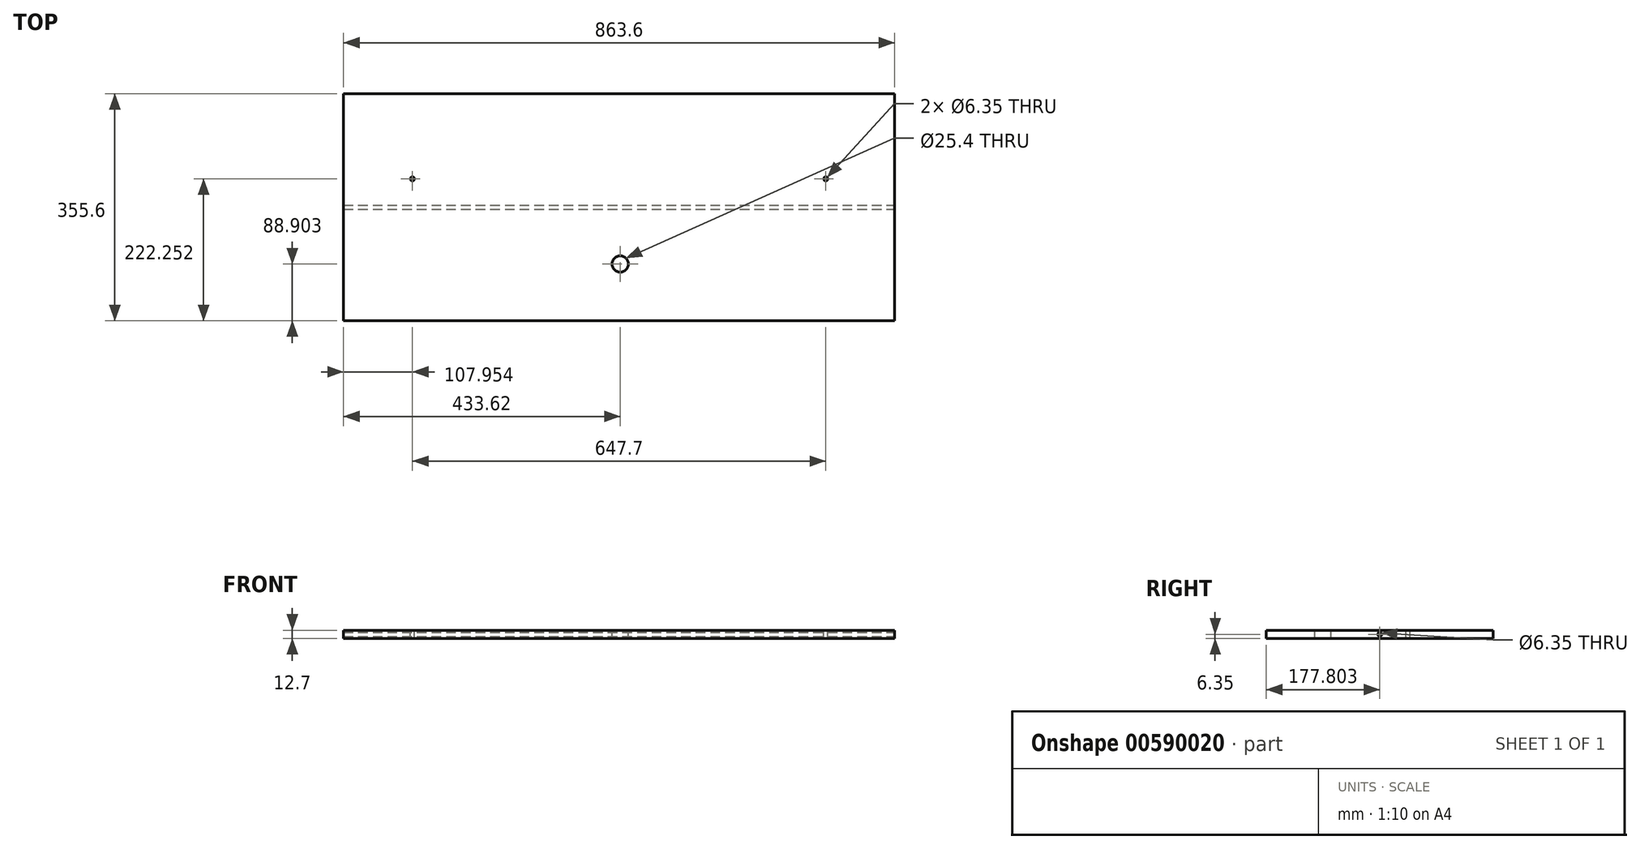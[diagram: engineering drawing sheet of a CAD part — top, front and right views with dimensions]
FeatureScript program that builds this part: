
annotation { "Feature Type Name" : "Feature", "Feature Type Description" : "" }
export const myFeature = defineFeature(function(context is Context, id is Id, definition is map)
    precondition{}
    {
        {
            var Q0;
            Q0=qCreatedBy(makeId("Top.planeOp"),FACE);
            var sketch = newSketch(context, id + "F0", { "sketchPlane" : qUnion([Q0])});
            skLineSegment(sketch, "E0.bottom", {"start": v(-433.62, 199.8) * mm, "end": v(429.98, 199.8) * mm});
            skLineSegment(sketch, "E0.top", {"start": v(-433.62, -155.8) * mm, "end": v(429.98, -155.8) * mm});
            skLineSegment(sketch, "E0.left", {"start": v(-433.62, 199.8) * mm, "end": v(-433.62, -155.8) * mm});
            skLineSegment(sketch, "E0.right", {"start": v(429.98, 199.8) * mm, "end": v(429.98, -155.8) * mm});
            skSolve(sketch);
        }
        {
            var Q0;
            Q0=qSketchRegion(id+"F0",true);
            extrude(context, id + "F1", {"entities" : qUnion([Q0]), "depth" : 12.7 * mm, "offsetDistance" : 25.4 * mm});
        }
        {
            var Q0;
            Q0=makeQuery(id+"F1.opExtrude","SWEPT_FACE",FACE,{"disambiguationData":[OSD([sQuery(id+"F0.wireOp",EDGE,"E0.right")])]});
            var sketch = newSketch(context, id + "F2", { "sketchPlane" : qUnion([Q0])});
            skLineSegment(sketch, "E1", {"start": v(-155.8, 6.35) * mm, "end": v(199.8, 6.35) * mm, "construction": true});
            skLineSegment(sketch, "E2", {"start": v(22, 12.7) * mm, "end": v(22, 0) * mm, "construction": true});
            skCircle(sketch, "E3", {"center": v(22, 6.35) * mm, "radius": 3.18 * mm});
            skSolve(sketch);
        }
        {
            var Q0;
            Q0=qSketchRegion(id+"F2",true);
            extrude(context, id + "F3", {"entities" : qUnion([Q0]), "operationType" : NewBodyOperationType.REMOVE, "endBound" : BoundingType.THROUGH_ALL, "oppositeDirection" : true, "depth" : 25.4 * mm, "offsetDistance" : 25.4 * mm});
        }
        {
            var Q0;
            Q0=makeQuery(id+"F1.opExtrude","CAP_FACE",FACE,{"disambiguationData":[OSD([sQuery(id+"F0.wireOp",EDGE,"E0.bottom"),sQuery(id+"F0.wireOp",EDGE,"E0.top"),sQuery(id+"F0.wireOp",EDGE,"E0.left"),sQuery(id+"F0.wireOp",EDGE,"E0.right")])],"isStart":false});
            var sketch = newSketch(context, id + "F4", { "sketchPlane" : qUnion([Q0])});
            skLineSegment(sketch, "E4", {"start": v(-1.82, 199.8) * mm, "end": v(0, -155.8) * mm, "construction": true});
            skLineSegment(sketch, "E5", {"start": v(-1.82, 199.8) * mm, "end": v(429.98, 199.8) * mm, "construction": true});
            skLineSegment(sketch, "E6", {"start": v(429.98, 199.8) * mm, "end": v(214.08, 199.8) * mm, "construction": true});
            skLineSegment(sketch, "E7", {"start": v(214.08, 199.8) * mm, "end": v(214.08, -155.8) * mm, "construction": true});
            skLineSegment(sketch, "E8", {"start": v(-1.82, 199.8) * mm, "end": v(-433.62, 199.8) * mm, "construction": true});
            skLineSegment(sketch, "E9", {"start": v(-433.62, 199.8) * mm, "end": v(-217.72, 199.8) * mm, "construction": true});
            skLineSegment(sketch, "E10", {"start": v(-217.72, 199.8) * mm, "end": v(-217.72, -155.8) * mm, "construction": true});
            skLineSegment(sketch, "E11", {"start": v(-433.62, 22) * mm, "end": v(-433.62, -155.8) * mm, "construction": true});
            skLineSegment(sketch, "E12", {"start": v(-433.62, -155.8) * mm, "end": v(-433.62, -66.9) * mm, "construction": true});
            skLineSegment(sketch, "E13", {"start": v(-433.62, -66.9) * mm, "end": v(429.98, -66.9) * mm, "construction": true});
            skLineSegment(sketch, "E14", {"start": v(-433.62, 22) * mm, "end": v(-433.62, 199.8) * mm, "construction": true});
            skLineSegment(sketch, "E15", {"start": v(-433.62, 110.9) * mm, "end": v(429.98, 110.9) * mm, "construction": true});
            skLineSegment(sketch, "E16", {"start": v(-325.67, 199.8) * mm, "end": v(-325.67, 110.9) * mm, "construction": true});
            skLineSegment(sketch, "E17", {"start": v(-325.67, -155.8) * mm, "end": v(429.98, -155.8) * mm, "construction": true});
            skLineSegment(sketch, "E18", {"start": v(429.98, -155.8) * mm, "end": v(429.98, 199.8) * mm, "construction": true});
            skLineSegment(sketch, "E19", {"start": v(214.08, 199.8) * mm, "end": v(429.98, 199.8) * mm, "construction": true});
            skLineSegment(sketch, "E20", {"start": v(322.03, 199.8) * mm, "end": v(322.03, 110.9) * mm, "construction": true});
            skCircle(sketch, "E21", {"center": v(0, -66.9) * mm, "radius": 12.7 * mm});
            skPoint(sketch, "E21.centerSnap0", {"position": v(-1.82, -66.9) * mm});
            skLineSegment(sketch, "E22.trimOffspring", {"start": v(-217.72, 22) * mm, "end": v(214.08, 22) * mm, "construction": true});
            skLineSegment(sketch, "E23.trimOffspring", {"start": v(-325.67, -66.9) * mm, "end": v(-325.67, -155.8) * mm, "construction": true});
            skPoint(sketch, "E24.orphan", {"position": v(429.98, 22) * mm});
            skLineSegment(sketch, "E25.trimOffspring", {"start": v(322.03, -66.9) * mm, "end": v(322.03, -155.8) * mm, "construction": true});
            skLineSegment(sketch, "E26", {"start": v(-433.62, 22) * mm, "end": v(-217.72, 22) * mm, "construction": true});
            skLineSegment(sketch, "E27", {"start": v(214.08, 22) * mm, "end": v(429.98, 22) * mm, "construction": true});
            skLineSegment(sketch, "E28", {"start": v(214.08, 22) * mm, "end": v(214.08, 110.9) * mm, "construction": true});
            skLineSegment(sketch, "E29", {"start": v(214.08, 110.9) * mm, "end": v(429.98, 110.9) * mm, "construction": true});
            skLineSegment(sketch, "E30", {"start": v(429.98, 22) * mm, "end": v(214.08, 22) * mm, "construction": true});
            skLineSegment(sketch, "E31", {"start": v(-217.72, 22) * mm, "end": v(-433.62, 22) * mm, "construction": true});
            skLineSegment(sketch, "E32", {"start": v(-433.62, 22) * mm, "end": v(-433.62, 110.9) * mm, "construction": true});
            skLineSegment(sketch, "E33", {"start": v(-433.62, 110.9) * mm, "end": v(-217.72, 110.9) * mm, "construction": true});
            skLineSegment(sketch, "E34", {"start": v(-217.72, 22) * mm, "end": v(-217.72, 110.9) * mm, "construction": true});
            skCircle(sketch, "E35", {"center": v(-325.67, 66.45) * mm, "radius": 3.18 * mm});
            skPoint(sketch, "E35.centerSnap0", {"position": v(-217.72, 66.45) * mm});
            skPoint(sketch, "E35.centerSnap1", {"position": v(-325.67, 22) * mm});
            skCircle(sketch, "E36", {"center": v(322.03, 66.45) * mm, "radius": 3.18 * mm});
            skPoint(sketch, "E36.centerSnap0", {"position": v(214.08, 66.45) * mm});
            skSolve(sketch);
        }
        {
            var Q0;
            Q0=makeQuery(id+"F4.imprint","IMPRINT",FACE,{"disambiguationData":[TD([[makeQuery(id+"F4.imprint","IMPRINT",EDGE,{"derivedFrom":sQuery(id+"F4.wireOp",EDGE,"E21")}),1.0]])]});
            var Q1;
            Q1=sQuery(id+"F4.wireOp",EDGE,"E21");
            extrude(context, id + "F5", {"entities" : qUnion([Q0]), "operationType" : NewBodyOperationType.REMOVE, "surfaceEntities" : qUnion([Q1]), "oppositeDirection" : true, "depth" : 25.4 * mm, "offsetDistance" : 25.4 * mm});
        }
        {
            var Q0;
            Q0=qSketchRegion(id+"F4",true);
            extrude(context, id + "F6", {"entities" : qUnion([Q0]), "operationType" : NewBodyOperationType.REMOVE, "endBound" : BoundingType.THROUGH_ALL, "oppositeDirection" : true, "depth" : 25.4 * mm, "offsetDistance" : 25.4 * mm});
        }
    });
